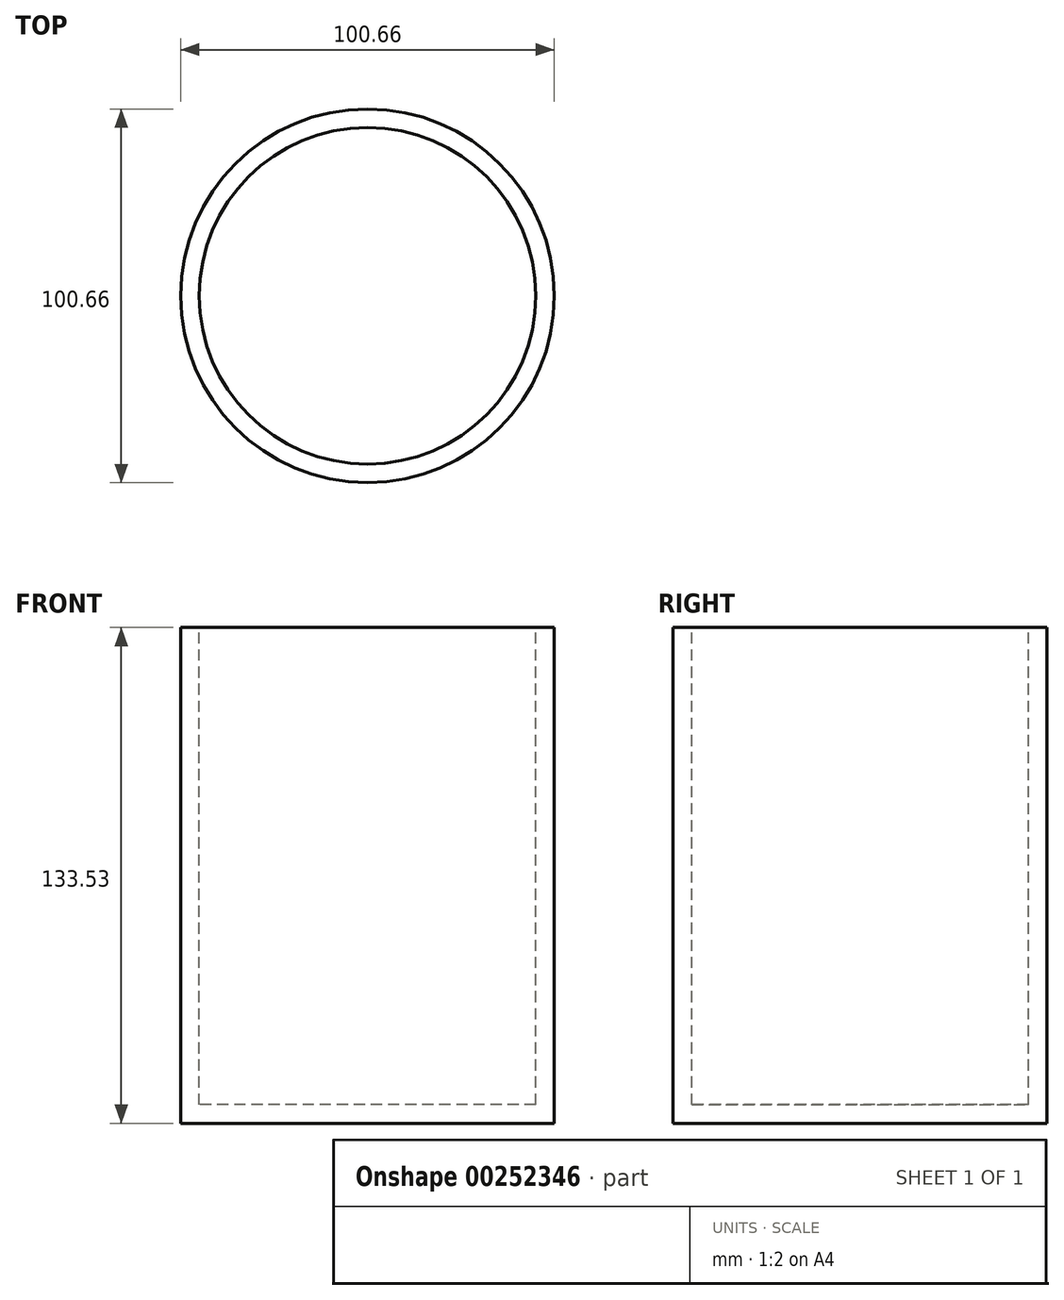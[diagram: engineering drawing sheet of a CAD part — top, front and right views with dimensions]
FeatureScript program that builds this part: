
annotation { "Feature Type Name" : "Feature", "Feature Type Description" : "" }
export const myFeature = defineFeature(function(context is Context, id is Id, definition is map)
    precondition{}
    {
        {
            var Q0;
            Q0=qCreatedBy(makeId("Front.planeOp"),FACE);
            var sketch = newSketch(context, id + "F0", { "sketchPlane" : qUnion([Q0])});
            skLineSegment(sketch, "E0.bottom", {"start": v(-45.33, 56.09) * mm, "end": v(46.48, 56.09) * mm});
            skLineSegment(sketch, "E0.top", {"start": v(-45.33, -72.44) * mm, "end": v(46.48, -72.44) * mm});
            skLineSegment(sketch, "E0.left", {"start": v(-45.33, 56.09) * mm, "end": v(-45.33, -72.44) * mm});
            skLineSegment(sketch, "E0.right", {"start": v(46.48, 56.09) * mm, "end": v(46.48, -72.44) * mm});
            skLineSegment(sketch, "E1", {"start": v(0, 56.09) * mm, "end": v(0, -72.44) * mm});
            skPoint(sketch, "E1.startSnap0", {"position": v(0.57, 56.09) * mm});
            skSolve(sketch);
        }
        {
            var Q0;
            {var subQ0=sQuery(id+"F0.wireOp",EDGE,"E0.left");Q0=makeQuery(id+"F0.imprint","IMPRINT",FACE,{"disambiguationData":[TD([[makeQuery(id+"F0.imprint","IMPRINT",EDGE,{"derivedFrom":subQ0}),1.0]])]});}
            var Q1;
            Q1=sQuery(id+"F0.wireOp",EDGE,"E1");
            revolve(context, id + "F1", {"entities" : qUnion([Q0]), "axis" : qUnion([Q1]), "revolveType" : RevolveType.FULL});
        }
        {
            var Q0;
            Q0=makeQuery(id+"F1.opRevolve","SWEPT_FACE",FACE,{"disambiguationData":[OSD([sQuery(id+"F0.wireOp",EDGE,"E0.bottom")])]});
            shell(context, id + "F2", {"entities" : qUnion([Q0]), "thickness" : 5 * mm, "oppositeDirection" : true});
        }
    });
